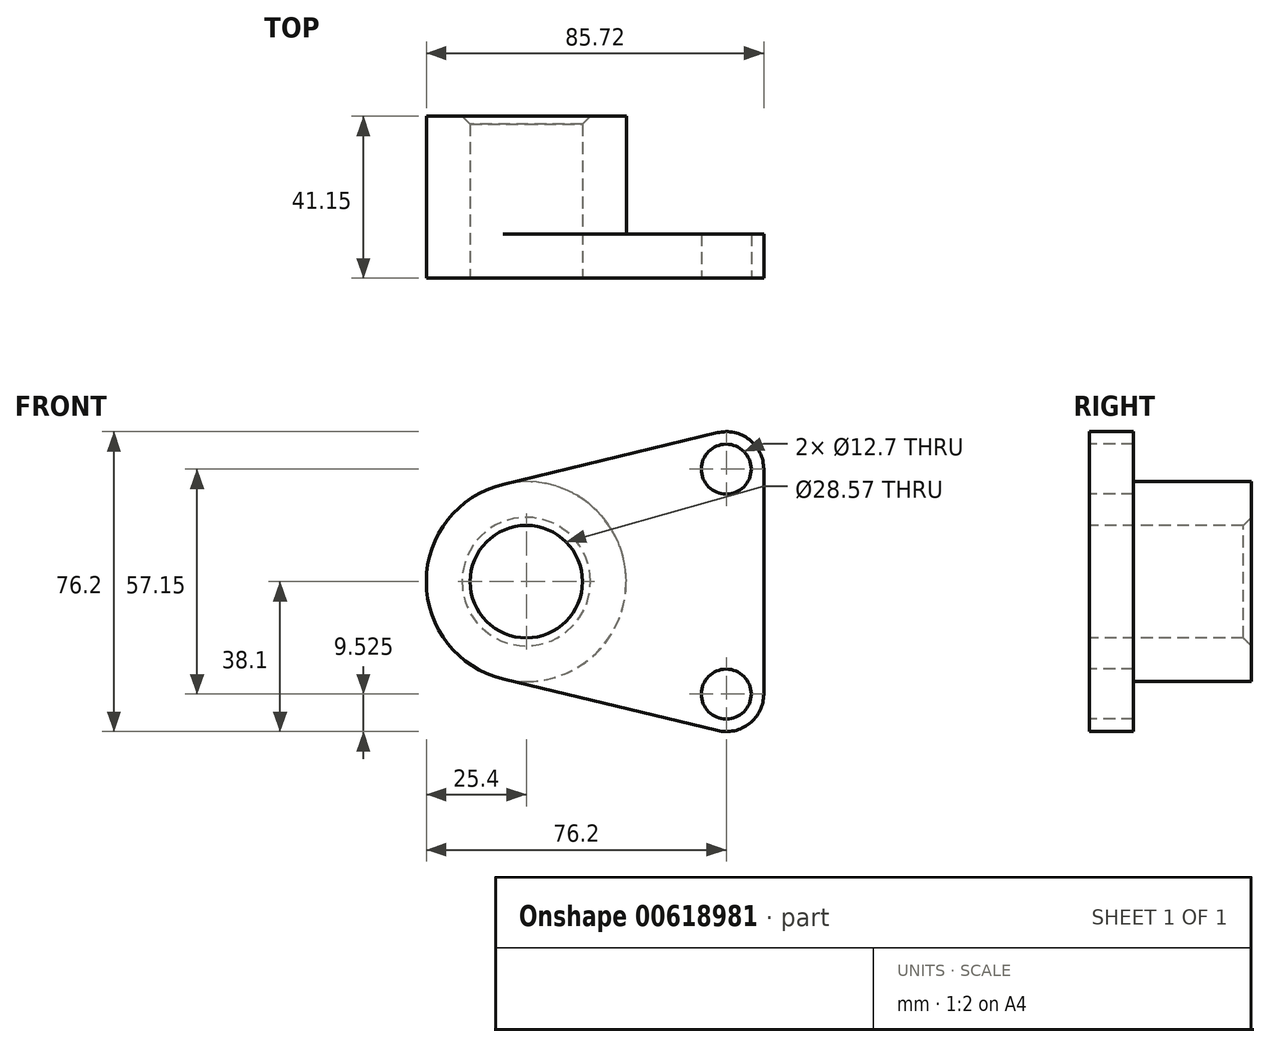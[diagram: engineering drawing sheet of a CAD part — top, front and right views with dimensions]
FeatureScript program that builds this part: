
annotation { "Feature Type Name" : "Feature", "Feature Type Description" : "" }
export const myFeature = defineFeature(function(context is Context, id is Id, definition is map)
    precondition{}
    {
        {
            var Q0;
            Q0=qCreatedBy(makeId("Front.planeOp"),FACE);
            var sketch = newSketch(context, id + "F0", { "sketchPlane" : qUnion([Q0])});
            skCircle(sketch, "E0", {"center": v(0, 0) * mm, "radius": 25.4 * mm});
            skCircle(sketch, "E1", {"center": v(0, 0) * mm, "radius": 14.29 * mm});
            skArc(sketch, "E2", {"start": v(60.32, 28.58) * mm, "mid": v(56.7, 36.06) * mm, "end": v(48.57, 37.83) * mm});
            skArc(sketch, "E3", {"start": v(48.57, -37.83) * mm, "mid": v(56.7, -36.06) * mm, "end": v(60.33, -28.57) * mm});
            skLineSegment(sketch, "E4", {"start": v(-5.95, 24.7) * mm, "end": v(48.57, 37.83) * mm});
            skLineSegment(sketch, "E5", {"start": v(-5.95, -24.7) * mm, "end": v(48.57, -37.83) * mm});
            skLineSegment(sketch, "E6", {"start": v(60.32, 41.15) * mm, "end": v(60.32, -28.57) * mm});
            skCircle(sketch, "E7", {"center": v(50.8, 28.58) * mm, "radius": 6.35 * mm});
            skCircle(sketch, "E8", {"center": v(50.8, -28.57) * mm, "radius": 6.35 * mm});
            skSolve(sketch);
        }
        {
            var Q0;
            Q0=makeQuery(id+"F0.imprint","IMPRINT",FACE,{"disambiguationData":[TD([[makeQuery(id+"F0.imprint","IMPRINT",EDGE,{"derivedFrom":sQuery(id+"F0.wireOp",EDGE,"E1")}),-1.0]])]});
            extrude(context, id + "F1", {"entities" : qUnion([Q0]), "oppositeDirection" : true, "depth" : 41.15 * mm, "offsetDistance" : 25.4 * mm});
        }
        {
            var Q0;
            Q0 = qSketchRegion(id + "F0", true);
            var Q1;
            Q1=makeQuery(id+"F1.opExtrude","CAP_FACE",FACE,{"disambiguationData":[OSD([sQuery(id+"F0.wireOp",EDGE,"E0"),sQuery(id+"F0.wireOp",EDGE,"E1")])],"isStart":true});
            extrude(context, id + "F2", {"entities" : qUnion([Q0, Q1]), "operationType" : NewBodyOperationType.ADD, "oppositeDirection" : true, "depth" : 11.18 * mm, "offsetDistance" : 25.4 * mm});
        }
        {
            var Q0;
            Q0=makeQuery(id+"F1.opExtrude","CAP_EDGE",EDGE,{"disambiguationData":[OSD([sQuery(id+"F0.wireOp",EDGE,"E1")])],"isStart":false});
            chamfer(context, id + "F3", {"entities" : qUnion([Q0]), "chamferType" : ChamferType.OFFSET_ANGLE, "width" : 2.03 * mm, "oppositeDirection" : false, "angle" : 45 * degree, "tangentPropagation" : true});
        }
    });
